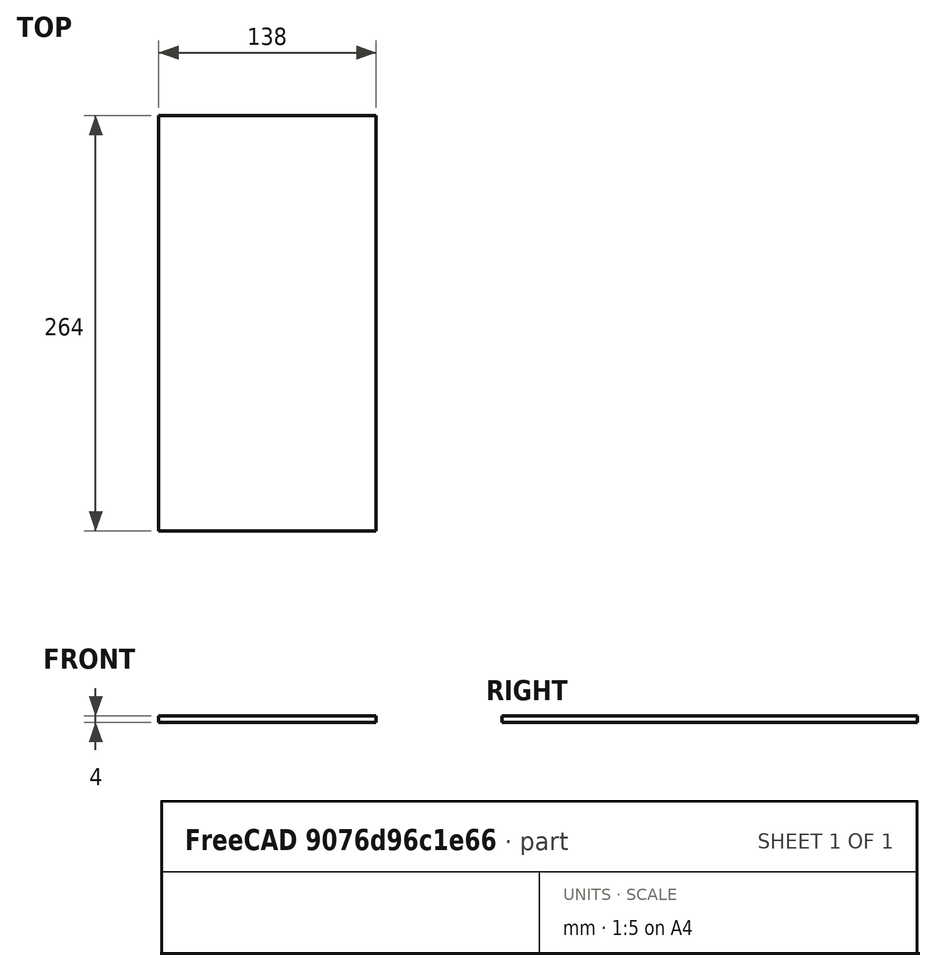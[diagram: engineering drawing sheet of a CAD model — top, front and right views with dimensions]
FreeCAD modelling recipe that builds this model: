
FCSTD DOCUMENT  (FreeCAD 1.0R39319 (Git))
Label: Shank_Shield
License: All rights reserved
LicenseURL: https://en.wikipedia.org/wiki/All_rights_reserved
objects: Sketcher::SketchObject×1, PartDesign::Pad×1, PartDesign::Body×1, PartDesign::CoordinateSystem×1, App::Part×1
note: 7 computed .brp shape members not serialized (recipe doc carries the construction recipe); baked Part::Feature solids carry a one-line shape summary decoded from their .brp

FEATURE [Sketcher::SketchObject] Sketch
  ArcFitTolerance = 1e-06
  AttachmentSupport = -> [XY_Plane001]
  FullyConstrained = true
  MakeInternals = false
  MapMode = 5
  sketch-geometry (4):
    g0: LineSegment StartX=0 StartY=0 StartZ=0 EndX=138 EndY=0 EndZ=0
    g1: LineSegment StartX=138 StartY=0 StartZ=0 EndX=138 EndY=264 EndZ=0
    g2: LineSegment StartX=138 StartY=264 StartZ=0 EndX=0 EndY=264 EndZ=0
    g3: LineSegment StartX=0 StartY=264 StartZ=0 EndX=0 EndY=0 EndZ=0
  constraints (11):
    c: Coincident(g0,g1)
    c: Coincident(g1,g2)
    c: Coincident(g2,g3)
    c: Coincident(g3,g0)
    c: Horizontal(g0)
    c: Horizontal(g2)
    c: Vertical(g1)
    c: Vertical(g3)
    c: Coincident(g0,g-1)
    c: DistanceX(g2,g2) = 138
    c: DistanceY(g1,g1) = 264
FEATURE [PartDesign::Pad] Pad
  Direction = (0,0,1)
  Length = 4
  Length2 = 10
  Profile = -> Sketch
  ReferenceAxis = -> Sketch [N_Axis]
  Refine = true
  Suppressed = false
  Type = 0
FEATURE [PartDesign::Body] Body  label="Shank_Shield001"
  AllowCompound = false
  Group = -> [Sketch,Pad]
  Origin = -> Origin001
  Tip = -> Pad
FEATURE [PartDesign::CoordinateSystem] LCS_1
  AttacherType = Attacher::AttachEngine3D
FEATURE [App::Part] Part  label="Shank_Shield"
  Group = -> [Body,LCS_1]
  Origin = -> Origin
